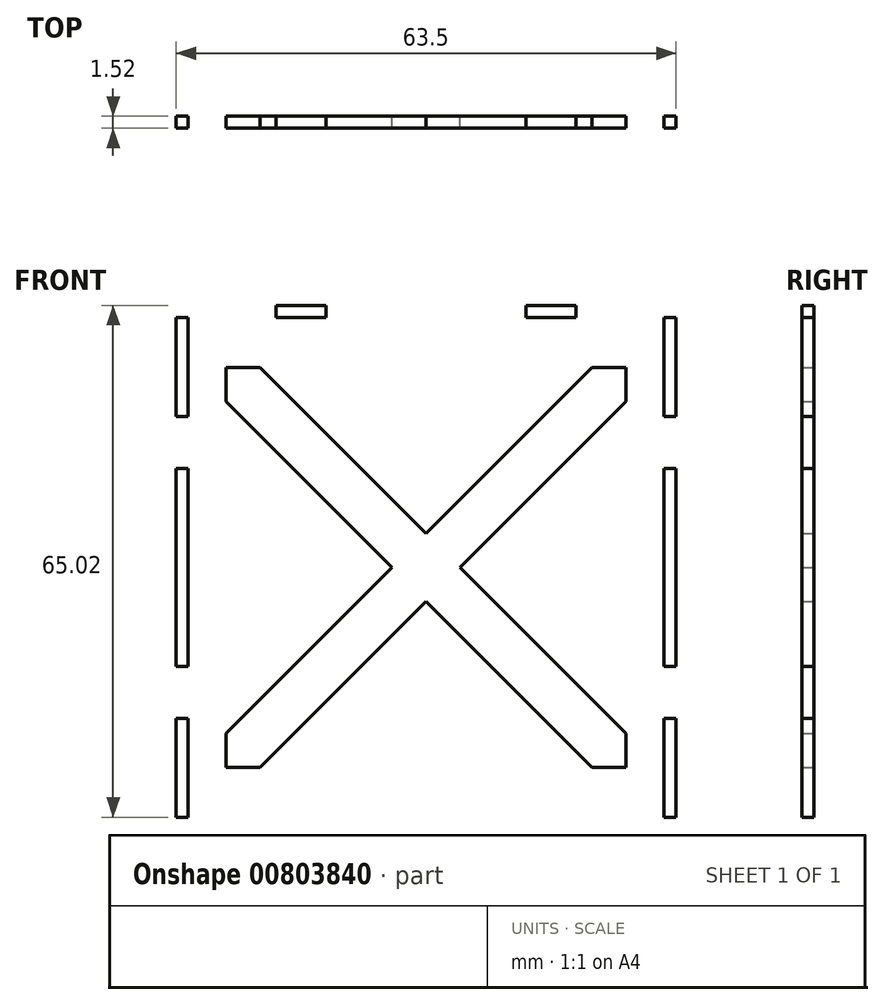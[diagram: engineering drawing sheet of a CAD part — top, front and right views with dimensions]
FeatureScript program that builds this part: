
annotation { "Feature Type Name" : "Feature", "Feature Type Description" : "" }
export const myFeature = defineFeature(function(context is Context, id is Id, definition is map)
    precondition{}
    {
        {
            var Q0;
            Q0=qCreatedBy(makeId("Front.planeOp"),FACE);
            var sketch = newSketch(context, id + "F0", { "sketchPlane" : qUnion([Q0])});
            skLineSegment(sketch, "E0.bottom", {"start": v(31.75, 31.75) * mm, "end": v(-31.75, 31.75) * mm});
            skLineSegment(sketch, "E0.top", {"start": v(31.75, -31.75) * mm, "end": v(-31.75, -31.75) * mm});
            skLineSegment(sketch, "E0.left", {"start": v(31.75, 31.75) * mm, "end": v(31.75, -31.75) * mm});
            skLineSegment(sketch, "E0.right", {"start": v(-31.75, 31.75) * mm, "end": v(-31.75, -31.75) * mm});
            skPoint(sketch, "E0.middle", {"position": v(0, 0) * mm});
            skLineSegment(sketch, "E1.bottom", {"start": v(-19.05, -31.75) * mm, "end": v(-12.7, -31.75) * mm});
            skLineSegment(sketch, "E1.top", {"start": v(-19.05, -33.27) * mm, "end": v(-12.7, -33.27) * mm});
            skLineSegment(sketch, "E1.left", {"start": v(-19.05, -31.75) * mm, "end": v(-19.05, -33.27) * mm});
            skLineSegment(sketch, "E1.right", {"start": v(-12.7, -31.75) * mm, "end": v(-12.7, -33.27) * mm});
            skPoint(sketch, "E2", {"position": v(-15.88, -31.75) * mm});
            skLineSegment(sketch, "E3.MirrorCS", {"start": v(19.05, -31.75) * mm, "end": v(12.7, -31.75) * mm});
            skPoint(sketch, "E4.MirrorP", {"position": v(15.88, -31.75) * mm});
            skLineSegment(sketch, "E5.MirrorCS", {"start": v(19.05, -33.27) * mm, "end": v(12.7, -33.27) * mm});
            skLineSegment(sketch, "E6.MirrorCS", {"start": v(12.7, -31.75) * mm, "end": v(12.7, -33.27) * mm});
            skLineSegment(sketch, "E7.MirrorCS", {"start": v(19.05, -31.75) * mm, "end": v(19.05, -33.27) * mm});
            skLineSegment(sketch, "E8.bottom", {"start": v(-31.75, -19.18) * mm, "end": v(-30.23, -19.18) * mm});
            skLineSegment(sketch, "E8.top", {"start": v(-31.75, -12.57) * mm, "end": v(-30.23, -12.57) * mm});
            skLineSegment(sketch, "E8.left", {"start": v(-31.75, -19.18) * mm, "end": v(-31.75, -12.57) * mm});
            skLineSegment(sketch, "E8.right", {"start": v(-30.23, -19.18) * mm, "end": v(-30.23, -12.57) * mm});
            skPoint(sketch, "E9", {"position": v(-31.75, -15.88) * mm});
            skLineSegment(sketch, "E10.MirrorCS", {"start": v(-31.75, 19.18) * mm, "end": v(-30.23, 19.18) * mm});
            skPoint(sketch, "E11.MirrorP", {"position": v(-31.75, 15.88) * mm});
            skLineSegment(sketch, "E12.MirrorCS", {"start": v(-31.75, 12.57) * mm, "end": v(-30.23, 12.57) * mm});
            skLineSegment(sketch, "E13.MirrorCS", {"start": v(-31.75, 19.18) * mm, "end": v(-31.75, 12.57) * mm});
            skLineSegment(sketch, "E14.MirrorCS", {"start": v(-30.23, 19.18) * mm, "end": v(-30.23, 12.57) * mm});
            skLineSegment(sketch, "E15.MirrorCS", {"start": v(31.75, 19.18) * mm, "end": v(30.23, 19.18) * mm});
            skLineSegment(sketch, "E16.MirrorCS", {"start": v(31.75, -19.18) * mm, "end": v(30.23, -19.18) * mm});
            skLineSegment(sketch, "E17.MirrorCS", {"start": v(31.75, -12.57) * mm, "end": v(30.23, -12.57) * mm});
            skLineSegment(sketch, "E18.MirrorCS", {"start": v(31.75, 12.57) * mm, "end": v(30.23, 12.57) * mm});
            skLineSegment(sketch, "E19.MirrorCS", {"start": v(30.23, 19.18) * mm, "end": v(30.23, 12.57) * mm});
            skLineSegment(sketch, "E20.MirrorCS", {"start": v(30.23, -19.18) * mm, "end": v(30.23, -12.57) * mm});
            skLineSegment(sketch, "E21.MirrorCS", {"start": v(31.75, 19.18) * mm, "end": v(31.75, 12.57) * mm});
            skLineSegment(sketch, "E22.MirrorCS", {"start": v(31.75, -19.18) * mm, "end": v(31.75, -12.57) * mm});
            skPoint(sketch, "E23.MirrorP", {"position": v(31.75, 15.88) * mm});
            skPoint(sketch, "E24.MirrorP", {"position": v(31.75, -15.88) * mm});
            skLineSegment(sketch, "E25.0", {"start": v(-30.23, 31.75) * mm, "end": v(-30.23, -31.75) * mm});
            skLineSegment(sketch, "E26.MirrorCS", {"start": v(30.23, 31.75) * mm, "end": v(30.23, -31.75) * mm});
            skLineSegment(sketch, "E27.bottom", {"start": v(25.4, 25.4) * mm, "end": v(-25.4, 25.4) * mm});
            skLineSegment(sketch, "E27.top", {"start": v(25.4, -25.4) * mm, "end": v(-25.4, -25.4) * mm});
            skLineSegment(sketch, "E27.left", {"start": v(25.4, 25.4) * mm, "end": v(25.4, -25.4) * mm});
            skLineSegment(sketch, "E27.right", {"start": v(-25.4, 25.4) * mm, "end": v(-25.4, -25.4) * mm});
            skLineSegment(sketch, "E28", {"start": v(-25.4, -25.4) * mm, "end": v(25.4, 25.4) * mm, "construction": true});
            skLineSegment(sketch, "E29", {"start": v(-25.4, 25.4) * mm, "end": v(25.4, -25.4) * mm, "construction": true});
            skLineSegment(sketch, "E30.0", {"start": v(-27.56, 23.24) * mm, "end": v(23.24, -27.56) * mm});
            skLineSegment(sketch, "E31.0", {"start": v(-23.24, 27.56) * mm, "end": v(27.56, -23.24) * mm});
            skLineSegment(sketch, "E32.0", {"start": v(-23.24, -27.56) * mm, "end": v(27.56, 23.24) * mm});
            skLineSegment(sketch, "E33.0", {"start": v(-27.56, -23.24) * mm, "end": v(23.24, 27.56) * mm});
            skLineSegment(sketch, "E34.MirrorCS", {"start": v(-19.05, 31.75) * mm, "end": v(-19.05, 33.27) * mm});
            skLineSegment(sketch, "E35.MirrorCS", {"start": v(-12.7, 31.75) * mm, "end": v(-12.7, 33.27) * mm});
            skLineSegment(sketch, "E36.MirrorCS", {"start": v(12.7, 31.75) * mm, "end": v(12.7, 33.27) * mm});
            skLineSegment(sketch, "E37.MirrorCS", {"start": v(19.05, 31.75) * mm, "end": v(19.05, 33.27) * mm});
            skLineSegment(sketch, "E38.MirrorCS", {"start": v(-19.05, 31.75) * mm, "end": v(-12.7, 31.75) * mm});
            skLineSegment(sketch, "E39.MirrorCS", {"start": v(-19.05, 33.27) * mm, "end": v(-12.7, 33.27) * mm});
            skLineSegment(sketch, "E40.MirrorCS", {"start": v(19.05, 31.75) * mm, "end": v(12.7, 31.75) * mm});
            skLineSegment(sketch, "E41.MirrorCS", {"start": v(19.05, 33.27) * mm, "end": v(12.7, 33.27) * mm});
            skPoint(sketch, "E42.MirrorP", {"position": v(-15.88, 31.75) * mm});
            skPoint(sketch, "E43.MirrorP", {"position": v(15.88, 31.75) * mm});
            skSolve(sketch);
        }
        {
            var Q0;
            {var subQ8=sQuery(id+"F0.wireOp",EDGE,"E1.bottom");Q0=makeQuery(id+"F0.imprint","IMPRINT",FACE,{"disambiguationData":[TD([[makeQuery(id+"F0.imprint","IMPRINT",EDGE,{"derivedFrom":subQ8}),1.0]])]});}
            var Q1;
            {var subQ5=sQuery(id+"F0.wireOp",EDGE,"E10.MirrorCS");Q1=makeQuery(id+"F0.imprint","IMPRINT",FACE,{"disambiguationData":[TD([[makeQuery(id+"F0.imprint","IMPRINT",EDGE,{"derivedFrom":subQ5}),1.0]])]});}
            var Q2;
            {var subQ0=sQuery(id+"F0.wireOp",EDGE,"E8.top");Q2=makeQuery(id+"F0.imprint","IMPRINT",FACE,{"disambiguationData":[TD([[makeQuery(id+"F0.imprint","IMPRINT",EDGE,{"derivedFrom":subQ0}),1.0]])]});}
            var Q3;
            {var subQ5=sQuery(id+"F0.wireOp",EDGE,"E8.bottom");Q3=makeQuery(id+"F0.imprint","IMPRINT",FACE,{"disambiguationData":[TD([[makeQuery(id+"F0.imprint","IMPRINT",EDGE,{"derivedFrom":subQ5}),-1.0]])]});}
            var Q4;
            {var subQ5=sQuery(id+"F0.wireOp",EDGE,"E16.MirrorCS");Q4=makeQuery(id+"F0.imprint","IMPRINT",FACE,{"disambiguationData":[TD([[makeQuery(id+"F0.imprint","IMPRINT",EDGE,{"derivedFrom":subQ5}),1.0]])]});}
            var Q5;
            {var subQ0=sQuery(id+"F0.wireOp",EDGE,"E17.MirrorCS");Q5=makeQuery(id+"F0.imprint","IMPRINT",FACE,{"disambiguationData":[TD([[makeQuery(id+"F0.imprint","IMPRINT",EDGE,{"derivedFrom":subQ0}),-1.0]])]});}
            var Q6;
            {var subQ5=sQuery(id+"F0.wireOp",EDGE,"E15.MirrorCS");Q6=makeQuery(id+"F0.imprint","IMPRINT",FACE,{"disambiguationData":[TD([[makeQuery(id+"F0.imprint","IMPRINT",EDGE,{"derivedFrom":subQ5}),-1.0]])]});}
            var Q7;
            Q7=makeQuery(id+"F0.imprint","IMPRINT",FACE,{"disambiguationData":[TD([[makeQuery(id+"F0.imprint","IMPRINT",EDGE,{"derivedFrom":sQuery(id+"F0.wireOp",EDGE,"E3.MirrorCS")}),1.0]])]});
            var Q8;
            Q8=makeQuery(id+"F0.imprint","IMPRINT",FACE,{"disambiguationData":[TD([[makeQuery(id+"F0.imprint","IMPRINT",EDGE,{"derivedFrom":sQuery(id+"F0.wireOp",EDGE,"E1.bottom")}),-1.0]])]});
            var Q9;
            {var subQ1=sQuery(id+"F0.wireOp",EDGE,"E27.bottom");var subQ5=sQuery(id+"F0.wireOp",EDGE,"E27.right");var subQ6=makeQuery(id+"F0.imprint","INTERSECT",VERTEX,{"derivedFrom":[subQ1,subQ5]});Q9=makeQuery(id+"F0.imprint","IMPRINT",FACE,{"disambiguationData":[TD([[makeQuery(id+"F0.imprint","IMPRINT",EDGE,{"disambiguationData":[TD([[subQ6,1.0]])],"derivedFrom":subQ1}),1.0]])]});}
            var Q10;
            {var subQ0=sQuery(id+"F0.wireOp",EDGE,"E33.0");var subQ1=sQuery(id+"F0.wireOp",EDGE,"E30.0");var subQ2=makeQuery(id+"F0.imprint","INTERSECT",VERTEX,{"derivedFrom":[subQ1,subQ0]});Q10=makeQuery(id+"F0.imprint","IMPRINT",FACE,{"disambiguationData":[TD([[makeQuery(id+"F0.imprint","IMPRINT",EDGE,{"disambiguationData":[TD([[subQ2,-1.0]])],"derivedFrom":subQ1}),1.0]])]});}
            var Q11;
            {var subQ5=sQuery(id+"F0.wireOp",EDGE,"E27.left");var subQ6=sQuery(id+"F0.wireOp",EDGE,"E27.bottom");var subQ7=makeQuery(id+"F0.imprint","INTERSECT",VERTEX,{"derivedFrom":[subQ6,subQ5]});Q11=makeQuery(id+"F0.imprint","IMPRINT",FACE,{"disambiguationData":[TD([[makeQuery(id+"F0.imprint","IMPRINT",EDGE,{"disambiguationData":[TD([[subQ7,-1.0]])],"derivedFrom":subQ6}),1.0]])]});}
            var Q12;
            {var subQ1=sQuery(id+"F0.wireOp",EDGE,"E27.left");var subQ6=sQuery(id+"F0.wireOp",EDGE,"E27.top");var subQ9=makeQuery(id+"F0.imprint","INTERSECT",VERTEX,{"derivedFrom":[subQ6,subQ1]});Q12=makeQuery(id+"F0.imprint","IMPRINT",FACE,{"disambiguationData":[TD([[makeQuery(id+"F0.imprint","IMPRINT",EDGE,{"disambiguationData":[TD([[subQ9,-1.0]])],"derivedFrom":subQ6}),-1.0]])]});}
            var Q13;
            {var subQ1=sQuery(id+"F0.wireOp",EDGE,"E27.top");var subQ7=sQuery(id+"F0.wireOp",EDGE,"E27.right");var subQ8=makeQuery(id+"F0.imprint","INTERSECT",VERTEX,{"derivedFrom":[subQ1,subQ7]});Q13=makeQuery(id+"F0.imprint","IMPRINT",FACE,{"disambiguationData":[TD([[makeQuery(id+"F0.imprint","IMPRINT",EDGE,{"disambiguationData":[TD([[subQ8,1.0]])],"derivedFrom":subQ1}),-1.0]])]});}
            var Q14;
            Q14=makeQuery(id+"F0.imprint","IMPRINT",FACE,{"disambiguationData":[TD([[makeQuery(id+"F0.imprint","IMPRINT",EDGE,{"derivedFrom":sQuery(id+"F0.wireOp",EDGE,"E34.MirrorCS")}),-1.0]])]});
            var Q15;
            Q15=makeQuery(id+"F0.imprint","IMPRINT",FACE,{"disambiguationData":[TD([[makeQuery(id+"F0.imprint","IMPRINT",EDGE,{"derivedFrom":sQuery(id+"F0.wireOp",EDGE,"E36.MirrorCS")}),-1.0]])]});
            extrude(context, id + "F1", {"entities" : qUnion([Q0, Q1, Q2, Q3, Q4, Q5, Q6, Q7, Q8, Q9, Q10, Q11, Q12, Q13, Q14, Q15]), "depth" : 1.52 * mm, "offsetDistance" : 25.4 * mm});
        }
    });
